# Revit family: Door-Counter-Fire_FaceOfWallMount_Cookson
name_source: partatom
category: Doors
revit_build: Autodesk Revit 2013 (Build: 20121003_2115(x64)
units: mm (PartAtom-declared; Revit-internal decimal feet)

## types (6) — shared parameters
04 CSI = 08 33 00
95 CSI = 08330
Assembly Code = B2030410
Coil Dimension Note = 11” to 14” - Push Up Units may have different clearances / construction. Consult Cornell when dimensions are critical.
Cost Note = Based on size, materials selected. Consult Cookson.
Crank Height = 5' - 4"
Description = Rated shutters secure openings above counters in fire rated walls. Can fully close to the floor.
Distributor Locator = http://www.cooksondoor.com
Facia = Yes
From Coil Side Operate on Left = No
From Coil Side Operate on Right = Yes
Function = Interior
Height = 8' - 0"
Jamb Dimension Note = 2 3/4” wide. Consult Cornell when dimensions are critical.
Jamb Height = 8' - 4"
LEED Information = http://www.cooksondoor.com
Listings = UL Classified 3, 1 ½, 1 and ¾ hour labels. Factory Mutual approval listing.
Manufacturer = CornellCookson,Inc.
Model = ERC10
Mounting = Face of Wall
Operator Width = 7' - 4"
Optional Powder Coat Finish = No
Product Options = Rated Countertops by Cornell, Rated Integral Frame and Countertop Units, UL Classified smoke control.
Representatives Disclaimer = Cookson products are sold and installed through a nationwide network of independent distributors.
Revit Object Download Link = http://cornellcookson.smartbim.com
Sizing Disclaimer = Up to 16' wide when height is 7' 6” or less. To 12' wide when height is 10' or less.
Smoke Control = UL leakage rated assembly “S” label available.
Subcategory = Roll Up
URL = www.cooksondoor.com/product/counter-fire-shutter
URL CAD = http://www.cooksondoor.com
URL Photographs = www.cooksondoor.com/product/counter-fire-shutter
URL Specifications = http://www.cooksondoor.com
Wall Closure = By host
Wall Construction = Masonry, structural steel, fire-rated drywall
Width = 6' - 0"
zero-valued in all types: Cost

## per-type parameters (varying)
| type | Bottom Bar | Curtain 1 1/2" Slat | Facia Meterial | Guides | Hand Crank | Hood | Motor | Offset from Guide | Operator |
| Push-Up Operated, Galvanized Steel | Galvanized or powder coated plain steel (non curtain components) | Galvanized steel (curtain only) | Galvanized or powder coated plain steel (non curtain components) | Galvanized or powder coated plain steel (non curtain components) | No | Galvanized or powder coated plain steel (non curtain components) | No | 0' - 0" | Operator : M100 Motor Op. System |
| M100 Hand Crank Op. System, Galvanized Steel | Galvanized or powder coated plain steel (non curtain components) | Galvanized steel (curtain only) | Galvanized or powder coated plain steel (non curtain components) | Galvanized or powder coated plain steel (non curtain components) | Yes | Galvanized or powder coated plain steel (non curtain components) | No | 0' - 0" | Operator : M100 Hand Crank Op. System |
| M100 Motor Op. System, Galvanized Steel | Galvanized or powder coated plain steel (non curtain components) | Galvanized steel (curtain only) | Galvanized or powder coated plain steel (non curtain components) | Galvanized or powder coated plain steel (non curtain components) | No | Galvanized or powder coated plain steel (non curtain components) | Yes | 0' - 0" | Operator : M100 Motor Op. System |
| Push-Up Operated, Stainless Steel | Stainless steel (non-curtain components) | Stainless steel (curtain only) | Stainless steel (non-curtain components) | Stainless steel (non-curtain components) | No | Stainless steel (non-curtain components) | No | 0' - 0" | Operator : Push-UP |
| M100 Motor Op. System, Stainless Steel | Stainless steel (non-curtain components) | Stainless steel (curtain only) | Stainless steel (non-curtain components) | Stainless steel (non-curtain components) | No | Stainless steel (non-curtain components) | Yes | 0' - 1 3/8" | Operator : M100 Motor Op. System |
| M100 Hand Crank Op. System, Stainless Steel | Stainless steel (non-curtain components) | Stainless steel (curtain only) | Stainless steel (non-curtain components) | Stainless steel (non-curtain components) | Yes | Stainless steel (non-curtain components) | No | 0' - 0" | Operator : M100 Hand Crank Op. System |

## geometry (parser evidence)
native form markers: Blend x18, Sweep x22
no freeform markers — native parametric forms only
